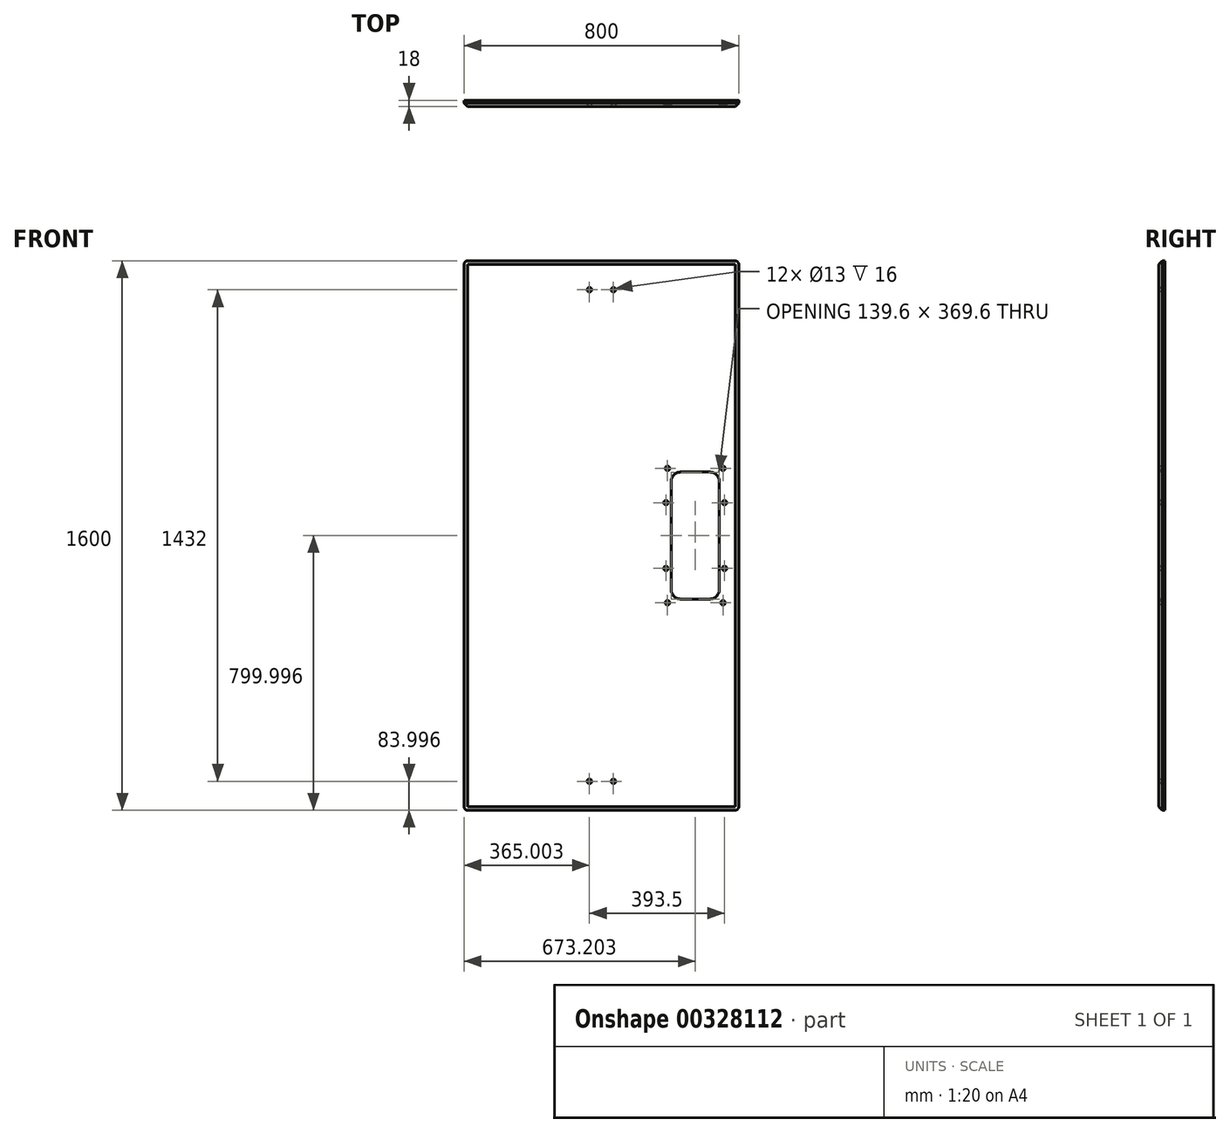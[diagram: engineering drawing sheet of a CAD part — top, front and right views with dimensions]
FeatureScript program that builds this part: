
annotation { "Feature Type Name" : "Feature", "Feature Type Description" : "" }
export const myFeature = defineFeature(function(context is Context, id is Id, definition is map)
    precondition{}
    {
        {
            var Q0;
            Q0=qCreatedBy(makeId("Front.planeOp"),FACE);
            var sketch = newSketch(context, id + "F0", { "sketchPlane" : qUnion([Q0])});
            skLineSegment(sketch, "E0", {"start": v(183.64, 185.32) * mm, "end": v(183.64, -130.68) * mm});
            skArc(sketch, "E1", {"start": v(183.64, -130.68) * mm, "mid": v(175.8, -149.63) * mm, "end": v(156.84, -157.48) * mm});
            skLineSegment(sketch, "E2", {"start": v(156.84, -157.48) * mm, "end": v(70.84, -157.48) * mm});
            skArc(sketch, "E3", {"start": v(70.84, -157.48) * mm, "mid": v(51.9, -149.63) * mm, "end": v(44.04, -130.68) * mm});
            skLineSegment(sketch, "E4", {"start": v(44.04, -130.68) * mm, "end": v(44.04, 185.32) * mm});
            skArc(sketch, "E5", {"start": v(44.04, 185.32) * mm, "mid": v(51.9, 204.27) * mm, "end": v(70.84, 212.12) * mm});
            skLineSegment(sketch, "E6", {"start": v(70.84, 212.12) * mm, "end": v(156.84, 212.12) * mm});
            skArc(sketch, "E7", {"start": v(156.84, 212.12) * mm, "mid": v(175.8, 204.27) * mm, "end": v(183.64, 185.32) * mm});
            skArc(sketch, "E8", {"start": v(240.64, 817.32) * mm, "mid": v(237.71, 824.39) * mm, "end": v(230.64, 827.32) * mm});
            skLineSegment(sketch, "E9", {"start": v(230.64, 827.32) * mm, "end": v(-549.36, 827.32) * mm});
            skArc(sketch, "E10", {"start": v(-549.36, 827.32) * mm, "mid": v(-556.43, 824.39) * mm, "end": v(-559.36, 817.32) * mm});
            skLineSegment(sketch, "E11", {"start": v(-559.36, 817.32) * mm, "end": v(-559.36, -762.68) * mm});
            skArc(sketch, "E12", {"start": v(-559.36, -762.68) * mm, "mid": v(-556.43, -769.75) * mm, "end": v(-549.36, -772.68) * mm});
            skLineSegment(sketch, "E13", {"start": v(-549.36, -772.68) * mm, "end": v(230.64, -772.68) * mm});
            skArc(sketch, "E14", {"start": v(230.64, -772.68) * mm, "mid": v(237.71, -769.75) * mm, "end": v(240.64, -762.68) * mm});
            skLineSegment(sketch, "E15", {"start": v(240.64, -762.68) * mm, "end": v(240.64, 817.32) * mm});
            skCircle(sketch, "E16", {"center": v(-124.36, -688.68) * mm, "radius": 4.5 * mm});
            skCircle(sketch, "E17", {"center": v(-194.36, -688.68) * mm, "radius": 4.5 * mm});
            skCircle(sketch, "E18", {"center": v(-124.36, 743.32) * mm, "radius": 4.5 * mm});
            skCircle(sketch, "E19", {"center": v(-194.36, 743.32) * mm, "radius": 4.5 * mm});
            skCircle(sketch, "E20", {"center": v(28.54, 123.12) * mm, "radius": 4.5 * mm});
            skCircle(sketch, "E21", {"center": v(194.64, 223.12) * mm, "radius": 4.5 * mm});
            skCircle(sketch, "E22", {"center": v(194.64, -168.48) * mm, "radius": 4.5 * mm});
            skCircle(sketch, "E23", {"center": v(33.04, -168.48) * mm, "radius": 4.5 * mm});
            skCircle(sketch, "E24", {"center": v(33.04, 223.12) * mm, "radius": 4.5 * mm});
            skCircle(sketch, "E25", {"center": v(28.54, -68.48) * mm, "radius": 4.5 * mm});
            skCircle(sketch, "E26", {"center": v(199.14, -68.48) * mm, "radius": 4.5 * mm});
            skCircle(sketch, "E27", {"center": v(199.14, 123.12) * mm, "radius": 4.5 * mm});
            skCircle(sketch, "E28", {"center": v(-194.36, -688.68) * mm, "radius": 6.5 * mm});
            skCircle(sketch, "E29", {"center": v(199.14, -68.48) * mm, "radius": 6.5 * mm});
            skCircle(sketch, "E30", {"center": v(194.64, 223.12) * mm, "radius": 6.5 * mm});
            skCircle(sketch, "E31", {"center": v(28.54, 123.12) * mm, "radius": 6.5 * mm});
            skCircle(sketch, "E32", {"center": v(33.04, -168.48) * mm, "radius": 6.5 * mm});
            skCircle(sketch, "E33", {"center": v(28.54, -68.48) * mm, "radius": 6.5 * mm});
            skCircle(sketch, "E34", {"center": v(33.04, 223.12) * mm, "radius": 6.5 * mm});
            skCircle(sketch, "E35", {"center": v(199.14, 123.12) * mm, "radius": 6.5 * mm});
            skCircle(sketch, "E36", {"center": v(194.64, -168.48) * mm, "radius": 6.5 * mm});
            skCircle(sketch, "E37", {"center": v(-124.36, -688.68) * mm, "radius": 6.5 * mm});
            skCircle(sketch, "E38", {"center": v(-124.36, 743.32) * mm, "radius": 6.5 * mm});
            skCircle(sketch, "E39", {"center": v(-194.36, 743.32) * mm, "radius": 6.5 * mm});
            skSolve(sketch);
        }
        {
            var Q0;
            Q0=makeQuery(id+"F0.imprint","IMPRINT",FACE,{"disambiguationData":[TD([[makeQuery(id+"F0.imprint","IMPRINT",EDGE,{"derivedFrom":sQuery(id+"F0.wireOp",EDGE,"E16")}),1.0]])]});
            var Q1;
            Q1=makeQuery(id+"F0.imprint","IMPRINT",FACE,{"disambiguationData":[TD([[makeQuery(id+"F0.imprint","IMPRINT",EDGE,{"derivedFrom":sQuery(id+"F0.wireOp",EDGE,"E16")}),-1.0]])]});
            var Q2;
            Q2=makeQuery(id+"F0.imprint","IMPRINT",FACE,{"disambiguationData":[TD([[makeQuery(id+"F0.imprint","IMPRINT",EDGE,{"derivedFrom":sQuery(id+"F0.wireOp",EDGE,"E17")}),-1.0]])]});
            var Q3;
            Q3=makeQuery(id+"F0.imprint","IMPRINT",FACE,{"disambiguationData":[TD([[makeQuery(id+"F0.imprint","IMPRINT",EDGE,{"derivedFrom":sQuery(id+"F0.wireOp",EDGE,"E17")}),1.0]])]});
            var Q4;
            Q4=makeQuery(id+"F0.imprint","IMPRINT",FACE,{"disambiguationData":[TD([[makeQuery(id+"F0.imprint","IMPRINT",EDGE,{"derivedFrom":sQuery(id+"F0.wireOp",EDGE,"E22")}),-1.0]])]});
            var Q5;
            Q5=makeQuery(id+"F0.imprint","IMPRINT",FACE,{"disambiguationData":[TD([[makeQuery(id+"F0.imprint","IMPRINT",EDGE,{"derivedFrom":sQuery(id+"F0.wireOp",EDGE,"E22")}),1.0]])]});
            var Q6;
            Q6=makeQuery(id+"F0.imprint","IMPRINT",FACE,{"disambiguationData":[TD([[makeQuery(id+"F0.imprint","IMPRINT",EDGE,{"derivedFrom":sQuery(id+"F0.wireOp",EDGE,"E26")}),-1.0]])]});
            var Q7;
            Q7=makeQuery(id+"F0.imprint","IMPRINT",FACE,{"disambiguationData":[TD([[makeQuery(id+"F0.imprint","IMPRINT",EDGE,{"derivedFrom":sQuery(id+"F0.wireOp",EDGE,"E26")}),1.0]])]});
            var Q8;
            Q8=makeQuery(id+"F0.imprint","IMPRINT",FACE,{"disambiguationData":[TD([[makeQuery(id+"F0.imprint","IMPRINT",EDGE,{"derivedFrom":sQuery(id+"F0.wireOp",EDGE,"E23")}),-1.0]])]});
            var Q9;
            Q9=makeQuery(id+"F0.imprint","IMPRINT",FACE,{"disambiguationData":[TD([[makeQuery(id+"F0.imprint","IMPRINT",EDGE,{"derivedFrom":sQuery(id+"F0.wireOp",EDGE,"E23")}),1.0]])]});
            var Q10;
            Q10=makeQuery(id+"F0.imprint","IMPRINT",FACE,{"disambiguationData":[TD([[makeQuery(id+"F0.imprint","IMPRINT",EDGE,{"derivedFrom":sQuery(id+"F0.wireOp",EDGE,"E25")}),-1.0]])]});
            var Q11;
            Q11=makeQuery(id+"F0.imprint","IMPRINT",FACE,{"disambiguationData":[TD([[makeQuery(id+"F0.imprint","IMPRINT",EDGE,{"derivedFrom":sQuery(id+"F0.wireOp",EDGE,"E25")}),1.0]])]});
            var Q12;
            Q12=makeQuery(id+"F0.imprint","IMPRINT",FACE,{"disambiguationData":[TD([[makeQuery(id+"F0.imprint","IMPRINT",EDGE,{"derivedFrom":sQuery(id+"F0.wireOp",EDGE,"E20")}),-1.0]])]});
            var Q13;
            Q13=makeQuery(id+"F0.imprint","IMPRINT",FACE,{"disambiguationData":[TD([[makeQuery(id+"F0.imprint","IMPRINT",EDGE,{"derivedFrom":sQuery(id+"F0.wireOp",EDGE,"E20")}),1.0]])]});
            var Q14;
            Q14=makeQuery(id+"F0.imprint","IMPRINT",FACE,{"disambiguationData":[TD([[makeQuery(id+"F0.imprint","IMPRINT",EDGE,{"derivedFrom":sQuery(id+"F0.wireOp",EDGE,"E27")}),-1.0]])]});
            var Q15;
            Q15=makeQuery(id+"F0.imprint","IMPRINT",FACE,{"disambiguationData":[TD([[makeQuery(id+"F0.imprint","IMPRINT",EDGE,{"derivedFrom":sQuery(id+"F0.wireOp",EDGE,"E27")}),1.0]])]});
            var Q16;
            Q16=makeQuery(id+"F0.imprint","IMPRINT",FACE,{"disambiguationData":[TD([[makeQuery(id+"F0.imprint","IMPRINT",EDGE,{"derivedFrom":sQuery(id+"F0.wireOp",EDGE,"E21")}),-1.0]])]});
            var Q17;
            Q17=makeQuery(id+"F0.imprint","IMPRINT",FACE,{"disambiguationData":[TD([[makeQuery(id+"F0.imprint","IMPRINT",EDGE,{"derivedFrom":sQuery(id+"F0.wireOp",EDGE,"E21")}),1.0]])]});
            var Q18;
            Q18=makeQuery(id+"F0.imprint","IMPRINT",FACE,{"disambiguationData":[TD([[makeQuery(id+"F0.imprint","IMPRINT",EDGE,{"derivedFrom":sQuery(id+"F0.wireOp",EDGE,"E24")}),-1.0]])]});
            var Q19;
            Q19=makeQuery(id+"F0.imprint","IMPRINT",FACE,{"disambiguationData":[TD([[makeQuery(id+"F0.imprint","IMPRINT",EDGE,{"derivedFrom":sQuery(id+"F0.wireOp",EDGE,"E24")}),1.0]])]});
            var Q20;
            Q20=makeQuery(id+"F0.imprint","IMPRINT",FACE,{"disambiguationData":[TD([[makeQuery(id+"F0.imprint","IMPRINT",EDGE,{"derivedFrom":sQuery(id+"F0.wireOp",EDGE,"E19")}),-1.0]])]});
            var Q21;
            Q21=makeQuery(id+"F0.imprint","IMPRINT",FACE,{"disambiguationData":[TD([[makeQuery(id+"F0.imprint","IMPRINT",EDGE,{"derivedFrom":sQuery(id+"F0.wireOp",EDGE,"E19")}),1.0]])]});
            var Q22;
            Q22=makeQuery(id+"F0.imprint","IMPRINT",FACE,{"disambiguationData":[TD([[makeQuery(id+"F0.imprint","IMPRINT",EDGE,{"derivedFrom":sQuery(id+"F0.wireOp",EDGE,"E18")}),-1.0]])]});
            var Q23;
            Q23=makeQuery(id+"F0.imprint","IMPRINT",FACE,{"disambiguationData":[TD([[makeQuery(id+"F0.imprint","IMPRINT",EDGE,{"derivedFrom":sQuery(id+"F0.wireOp",EDGE,"E18")}),1.0]])]});
            var Q24;
            Q24=makeQuery(id+"F0.imprint","IMPRINT",FACE,{"disambiguationData":[TD([[makeQuery(id+"F0.imprint","IMPRINT",EDGE,{"derivedFrom":sQuery(id+"F0.wireOp",EDGE,"E0")}),1.0]])]});
            extrude(context, id + "F1", {"entities" : qUnion([Q0, Q1, Q2, Q3, Q4, Q5, Q6, Q7, Q8, Q9, Q10, Q11, Q12, Q13, Q14, Q15, Q16, Q17, Q18, Q19, Q20, Q21, Q22, Q23, Q24]), "oppositeDirection" : true, "depth" : 18 * mm});
        }
        {
            var Q0;
            Q0=makeQuery(id+"F0.imprint","IMPRINT",FACE,{"disambiguationData":[TD([[makeQuery(id+"F0.imprint","IMPRINT",EDGE,{"derivedFrom":sQuery(id+"F0.wireOp",EDGE,"E17")}),-1.0]])]});
            var Q1;
            Q1=makeQuery(id+"F0.imprint","IMPRINT",FACE,{"disambiguationData":[TD([[makeQuery(id+"F0.imprint","IMPRINT",EDGE,{"derivedFrom":sQuery(id+"F0.wireOp",EDGE,"E16")}),-1.0]])]});
            var Q2;
            Q2=makeQuery(id+"F0.imprint","IMPRINT",FACE,{"disambiguationData":[TD([[makeQuery(id+"F0.imprint","IMPRINT",EDGE,{"derivedFrom":sQuery(id+"F0.wireOp",EDGE,"E23")}),-1.0]])]});
            var Q3;
            Q3=makeQuery(id+"F0.imprint","IMPRINT",FACE,{"disambiguationData":[TD([[makeQuery(id+"F0.imprint","IMPRINT",EDGE,{"derivedFrom":sQuery(id+"F0.wireOp",EDGE,"E22")}),-1.0]])]});
            var Q4;
            Q4=makeQuery(id+"F0.imprint","IMPRINT",FACE,{"disambiguationData":[TD([[makeQuery(id+"F0.imprint","IMPRINT",EDGE,{"derivedFrom":sQuery(id+"F0.wireOp",EDGE,"E25")}),-1.0]])]});
            var Q5;
            Q5=makeQuery(id+"F0.imprint","IMPRINT",FACE,{"disambiguationData":[TD([[makeQuery(id+"F0.imprint","IMPRINT",EDGE,{"derivedFrom":sQuery(id+"F0.wireOp",EDGE,"E26")}),-1.0]])]});
            var Q6;
            Q6=makeQuery(id+"F0.imprint","IMPRINT",FACE,{"disambiguationData":[TD([[makeQuery(id+"F0.imprint","IMPRINT",EDGE,{"derivedFrom":sQuery(id+"F0.wireOp",EDGE,"E20")}),-1.0]])]});
            var Q7;
            Q7=makeQuery(id+"F0.imprint","IMPRINT",FACE,{"disambiguationData":[TD([[makeQuery(id+"F0.imprint","IMPRINT",EDGE,{"derivedFrom":sQuery(id+"F0.wireOp",EDGE,"E24")}),-1.0]])]});
            var Q8;
            Q8=makeQuery(id+"F0.imprint","IMPRINT",FACE,{"disambiguationData":[TD([[makeQuery(id+"F0.imprint","IMPRINT",EDGE,{"derivedFrom":sQuery(id+"F0.wireOp",EDGE,"E27")}),-1.0]])]});
            var Q9;
            Q9=makeQuery(id+"F0.imprint","IMPRINT",FACE,{"disambiguationData":[TD([[makeQuery(id+"F0.imprint","IMPRINT",EDGE,{"derivedFrom":sQuery(id+"F0.wireOp",EDGE,"E21")}),-1.0]])]});
            var Q10;
            Q10=makeQuery(id+"F0.imprint","IMPRINT",FACE,{"disambiguationData":[TD([[makeQuery(id+"F0.imprint","IMPRINT",EDGE,{"derivedFrom":sQuery(id+"F0.wireOp",EDGE,"E19")}),-1.0]])]});
            var Q11;
            Q11=makeQuery(id+"F0.imprint","IMPRINT",FACE,{"disambiguationData":[TD([[makeQuery(id+"F0.imprint","IMPRINT",EDGE,{"derivedFrom":sQuery(id+"F0.wireOp",EDGE,"E18")}),-1.0]])]});
            extrude(context, id + "F2", {"entities" : qUnion([Q0, Q1, Q2, Q3, Q4, Q5, Q6, Q7, Q8, Q9, Q10, Q11]), "operationType" : NewBodyOperationType.REMOVE, "oppositeDirection" : true, "depth" : 16 * mm});
        }
        {
            var Q0;
            Q0=makeQuery(id+"F0.imprint","IMPRINT",FACE,{"disambiguationData":[TD([[makeQuery(id+"F0.imprint","IMPRINT",EDGE,{"derivedFrom":sQuery(id+"F0.wireOp",EDGE,"E19")}),1.0]])]});
            var Q1;
            Q1=makeQuery(id+"F0.imprint","IMPRINT",FACE,{"disambiguationData":[TD([[makeQuery(id+"F0.imprint","IMPRINT",EDGE,{"derivedFrom":sQuery(id+"F0.wireOp",EDGE,"E18")}),1.0]])]});
            var Q2;
            Q2=makeQuery(id+"F0.imprint","IMPRINT",FACE,{"disambiguationData":[TD([[makeQuery(id+"F0.imprint","IMPRINT",EDGE,{"derivedFrom":sQuery(id+"F0.wireOp",EDGE,"E24")}),1.0]])]});
            var Q3;
            Q3=makeQuery(id+"F0.imprint","IMPRINT",FACE,{"disambiguationData":[TD([[makeQuery(id+"F0.imprint","IMPRINT",EDGE,{"derivedFrom":sQuery(id+"F0.wireOp",EDGE,"E21")}),1.0]])]});
            var Q4;
            Q4=makeQuery(id+"F0.imprint","IMPRINT",FACE,{"disambiguationData":[TD([[makeQuery(id+"F0.imprint","IMPRINT",EDGE,{"derivedFrom":sQuery(id+"F0.wireOp",EDGE,"E27")}),1.0]])]});
            var Q5;
            Q5=makeQuery(id+"F0.imprint","IMPRINT",FACE,{"disambiguationData":[TD([[makeQuery(id+"F0.imprint","IMPRINT",EDGE,{"derivedFrom":sQuery(id+"F0.wireOp",EDGE,"E26")}),1.0]])]});
            var Q6;
            Q6=makeQuery(id+"F0.imprint","IMPRINT",FACE,{"disambiguationData":[TD([[makeQuery(id+"F0.imprint","IMPRINT",EDGE,{"derivedFrom":sQuery(id+"F0.wireOp",EDGE,"E22")}),1.0]])]});
            var Q7;
            Q7=makeQuery(id+"F0.imprint","IMPRINT",FACE,{"disambiguationData":[TD([[makeQuery(id+"F0.imprint","IMPRINT",EDGE,{"derivedFrom":sQuery(id+"F0.wireOp",EDGE,"E23")}),1.0]])]});
            var Q8;
            Q8=makeQuery(id+"F0.imprint","IMPRINT",FACE,{"disambiguationData":[TD([[makeQuery(id+"F0.imprint","IMPRINT",EDGE,{"derivedFrom":sQuery(id+"F0.wireOp",EDGE,"E25")}),1.0]])]});
            var Q9;
            Q9=makeQuery(id+"F0.imprint","IMPRINT",FACE,{"disambiguationData":[TD([[makeQuery(id+"F0.imprint","IMPRINT",EDGE,{"derivedFrom":sQuery(id+"F0.wireOp",EDGE,"E20")}),1.0]])]});
            var Q10;
            Q10=makeQuery(id+"F0.imprint","IMPRINT",FACE,{"disambiguationData":[TD([[makeQuery(id+"F0.imprint","IMPRINT",EDGE,{"derivedFrom":sQuery(id+"F0.wireOp",EDGE,"E17")}),1.0]])]});
            var Q11;
            Q11=makeQuery(id+"F0.imprint","IMPRINT",FACE,{"disambiguationData":[TD([[makeQuery(id+"F0.imprint","IMPRINT",EDGE,{"derivedFrom":sQuery(id+"F0.wireOp",EDGE,"E16")}),1.0]])]});
            extrude(context, id + "F3", {"entities" : qUnion([Q0, Q1, Q2, Q3, Q4, Q5, Q6, Q7, Q8, Q9, Q10, Q11]), "operationType" : NewBodyOperationType.REMOVE, "oppositeDirection" : true, "depth" : 1 * mm});
        }
        {
            var Q0;
            Q0=makeQuery(id+"F1.opExtrude","CAP_EDGE",EDGE,{"disambiguationData":[OSD([sQuery(id+"F0.wireOp",EDGE,"E13")])],"isStart":true});
            chamfer(context, id + "F4", {"entities" : qUnion([Q0]), "width" : 10 * mm, "tangentPropagation" : true});
        }
    });
